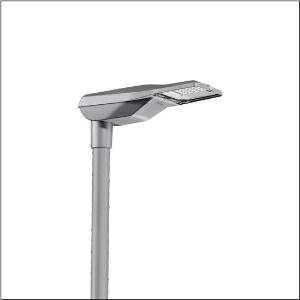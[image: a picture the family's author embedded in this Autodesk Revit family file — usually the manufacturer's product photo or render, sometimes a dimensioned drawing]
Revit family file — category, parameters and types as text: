
# Revit family: streetlight_sl_21_iq_micro___stw1_0a_5xe1e21g08cb_2b52
name_source: partatom
category: Lighting Fixtures
units: mm (PartAtom-declared; Revit-internal decimal feet)

## family parameters
Cut with Voids When Loaded = No
Host = Face
Light Source = No
Part Type = Normal
Room Calculation Point = No
Round Connector Dimension = Use Diameter
Shared = No

## types (1)
- --- (1 x LED, 2380 lm, 19.4 W, 2200K)
    Apparent Load = 19 VA
    CIE Flux Codes = 38 75 98 100 100
    Color Rendering = 70
    Color Temperature = 2200K
    Default Elevation = 1800 mm
    Description = Streetlight SL 21 iQ micro, mast luminaire, primary light control with lens, of PMMA, primary optical cover: cover, of toughened safety glass, transparent, light distribution: STW1.0a, light emission: direct distribution, primary light characteristic: asymmetric, installation type: post-top, side-entry, LED, High Power LED, rated luminous flux: 2.380lm, luminous efficacy: 123lm/W, light colour: 722, colour temperature: 2200K, control gear: iQ Street-Remote, control: Street-Remote, Auto-Match, Temp-Guard, Lumen-Switch, Night-Set, Smart-Wire, Light-Fading, Desk-Remote (wireless, voltage-free reading and setting of iQ features in the workshop via application-optimized NFC function/RFID function), optimised constant luminous flux control (CLO 2.0), pre-setting: linear dimming characteristic, mains connection: 220..240V, AC, 50/60Hz, start of lifetime: 19W, end of service life: 20W, reduction: 10W, luminaire housing, of diecast aluminium, powder-coated, Siteco® metallic grey (DB 702S), corrosivity category C5 high according to DIN EN ISO 12944, please order mast flange separately, inclination adjustable: 0°, 5°, 10°, 15°, sealing non-destructively replaceable, multi-level sealing system, length: 528mm, width: 235mm, height: 110mm, mast flange for spigot size: 42mm (side-entry): 5XC10008XM4, 60/48mm (side-entry/post-top): 5XC10108XM2, 76/60mm (side-entry/post-top): 5XC10108XM1, protection rating (complete): IP66, insulation class (complete): insulation class II (safety insulation), certification: CE, ENEC, ENEC+, VDE, impact resistance: IK10, permissible operating ambient temperature for outdoor applications: -40..+50°C, standard-compliant lighting for roads and squares, packaging unit: 1 piece

Light Distribution: STW1.0a
    Height = 110 mm
    Lamp = 1 x LED
    Lamp Light Flux = 2380 lm
    Lamp Power = 19.4 W
    Lamp count = 1
    Length = 528 mm
    Luminous efficacy = 123 lm/W
    Manufacturer = Siteco
    ModVariant = No
    Model = 5XE1E21G08CB
    Number of Poles = 1
    OnlyDefault = Yes
    Power Factor = 1
    Product Name = Streetlight SL 21 iQ micro | STW1.0a
    Product group = mast luminaire | pylon top
    ProductGroupID = 6100
    Protection Class = Protection class II
    Protection Degree = IP 66
    RLX_Detail_Level = 1
    RLX_Emergency_Light_Flux = 0 lm
    RLX_Emergency_Type = 0
    RLX_Emergency_Type_DB = No
    RlxData = <blob elided: 99105 chars, md5=638b6185>
    Socket = socket
    Standby Power = 0 W
    System Light Flux = 2380 lm
    System Power = 19 W
    Type Comments = factory setting: luminous flux: 100 % | dim-lin: 254 | 387 mA
    Type Image = l_1006881.jpg
    URL = http://relux.com
    VarID = @adj_142209
    Voltage = 0 V
    Weight = 0.00 kg
    Width = 235 mm

## geometry (parser evidence)
native form markers: Blend x4, Sweep x12
no freeform markers — native parametric forms only
